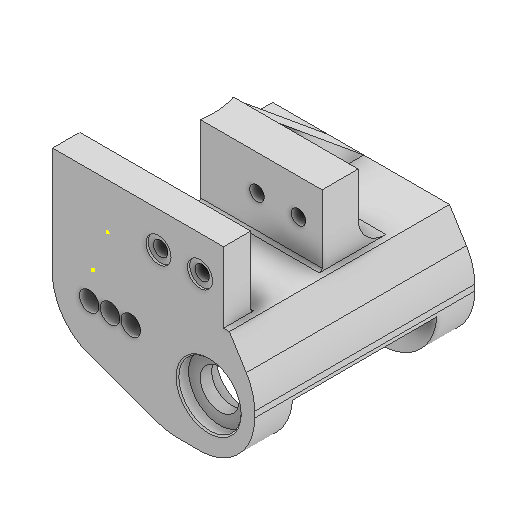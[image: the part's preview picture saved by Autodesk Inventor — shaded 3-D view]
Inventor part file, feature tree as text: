
AUTODESK INVENTOR PART (.ipt)
format: ipt  version: 2025 (Build 290162000, 162)  size: 635,392 bytes
history: native  units: in
note: dims shown in document units (in); Inventor stores cm internally (conversion verified against a paired STEP export)
features: sketch x34, extrude x32, projected_geometry x26, fillet x12, chamfer x3, reference x3, other x3, mirror x2, thicken_offset x1, plane x1, pattern_linear x1
ambient origin geometry x8: Origin, YZ Plane, XZ Plane, XY Plane, X Axis, Y Axis, Z Axis, Center Point
bodies: Solid1 (feature_tree)
feature tree (118):
  extrude  "Extrusion1"  Depth=0.25in
  extrude  "Extrusion2"  Depth=0.5512in
  extrude  "Extrusion7"  Depth=0.8809in
  extrude  "Extrusion10"  Depth=0.2165in TaperAngle=0.0deg
  extrude  "Extrusion11"  Depth=0.315in
  extrude  "Extrusion12"  TaperAngle=0.0deg  [1 undecoded]
  extrude  "Extrusion13"  Depth=0.3937in TaperAngle=0.0deg
  mirror  "Mirror1"
  fillet  "Fillet5"  Radius=0.3937in
  extrude  "Extrusion14"  Depth=0.3937in
  fillet  "Fillet6"  [1 undecoded]
  extrude  "Extrusion15"  Depth=0.3937in
  thicken_offset  "Thicken1"
  fillet  "Fillet7"  Radius=0.3858in
  extrude  "Extrusion16"  Depth=0.5118in
  extrude  "Extrusion17"  Depth=0.1969in
  fillet  "Fillet8"  Radius=1.0in
  extrude  "Extrusion18"  Depth=0.3937in
  extrude  "Extrusion19"  Depth=1.0in TaperAngle=0.0deg
  extrude  "Extrusion20"  Depth=0.315in
  extrude  "Extrusion21"  Depth=0.3228in
  extrude  "Extrusion22"  Depth=0.2756in
  extrude  "Extrusion23"  Depth=0.2047in
  plane  "Work Plane1"
  mirror  "Mirror2"
  fillet  "Fillet9"  Radius=0.2047in
  fillet  "Fillet10"  [1 undecoded]
  extrude  "Extrusion24"  Depth=0.3543in
  extrude  "Extrusion25"  Depth=0.7874in
  fillet  "Fillet12"  Radius=0.1969in
  fillet  "Fillet13"  Radius=0.1969in
  chamfer  "Chamfer1"  [1 undecoded]
  chamfer  "Chamfer2"  Distance=0.0197in Angle=45.0deg
  extrude  "Extrusion26"  Depth=0.3937in TaperAngle=0.0deg
  sketch  "Sketch27"  dims[d93=0.5in d94=0.0197in d95=0.0787in d96=45.0deg]
  extrude  "Extrusion27"  Depth=0.3937in TaperAngle=0.0deg
  extrude  "Extrusion28"  Depth=1.1811in
  extrude  "Extrusion29"  Depth=0.3937in TaperAngle=0.0deg
  pattern_linear  "Rectangular Pattern1"  Count1=2  [1 undecoded]
  extrude  "Extrusion30"  Depth=0.1969in
  extrude  "Extrusion31"  Depth=0.3937in TaperAngle=0.0deg
  extrude  "Extrusion32"  Depth=0.3937in TaperAngle=45.0deg
  fillet  "Fillet14"  Radius=0.0344in
  extrude  "Extrusion33"  TaperAngle=0.0deg  [1 undecoded]
  extrude  "Extrusion34"  TaperAngle=0.0deg  [1 undecoded]
  extrude  "Extrusion35"  TaperAngle=0.0deg  [1 undecoded]
  fillet  "Fillet15"  [1 undecoded]
  extrude  "Extrusion36"  TaperAngle=0.0deg  [1 undecoded]
  fillet  "Fillet16"  [1 undecoded]
  fillet  "Fillet18"  [1 undecoded]
  sketch  "Sketch39"  dims[d129=0.3937in d134=0.3937in d135=0.0in]
  extrude  "Extrusion38"  [1 undecoded]
  extrude  "Extrusion39"  [1 undecoded]
  chamfer  "Chamfer3"  [1 undecoded]
  sketch  "Sketch1"  dims[d1=1.005in d2=0.25in]
  sketch  "Sketch2"  dims[d3=2.0in d4=0.0in d5=0.5512in]
  projected_geometry  "Projected Loop1"
  sketch  "Sketch7"  dims[d6=0.0in d7=0.0in d21=0.8809in]
  sketch  "Sketch10"  dims[d22=0.1575in d23=0.0in d32=0.2165in d33=0.0in]
  projected_geometry  "Projected Loop7"
  sketch  "Sketch11"  dims[d34=1.1024in d35=0.315in]
  sketch  "Sketch12"  dims[d36=0.2047in d37=0.0in d38=0.0in]
  projected_geometry  "Projected Loop8"
  sketch  "Sketch13"  dims[d39=0.3937in d40=0.0in d42=1.0236in d43=0.0in d45=0.3937in]
  projected_geometry  "Projected Loop9"
  sketch  "Sketch14"  dims[d46=1.0236in d47=0.0in d48=0.3937in d49=0.0in d50=0.0in]
  projected_geometry  "Projected Loop10"
  sketch  "Sketch15"  dims[d51=0.0591in d52=0.1in d53=0.3937in d54=0.3858in]
  projected_geometry  "Projected Loop11"
  sketch  "Sketch16"  dims[d55=0.0079in d56=0.5118in]
  projected_geometry  "Projected Loop12"
  reference  "Reference1"
  sketch  "Sketch17"  dims[d57=0.2756in d58=0.1969in d59=1.0in d60=0.0in]
  projected_geometry  "Projected Loop13"
  sketch  "Sketch18"  dims[d61=1.0in d62=0.0in d63=0.3937in]
  projected_geometry  "Projected Loop14"
  reference  "Reference2"
  sketch  "Sketch19"  dims[d64=0.2047in d65=1.0in d66=0.0in]
  sketch  "Sketch20"  dims[d67=0.315in d68=0.315in]
  sketch  "Sketch21"  dims[d69=0.1969in d70=0.0in d71=0.3228in]
  sketch  "Sketch22"  dims[d72=0.315in d73=0.0in d74=0.2756in]
  reference  "Reference3"
  sketch  "Sketch23"  dims[d75=0.4724in d76=0.0in d77=0.2047in d78=0.2047in d79=0.0in d80=0.0in]
  projected_geometry  "Projected Loop15"
  sketch  "Sketch24"  dims[d81=0.3543in d82=0.3543in]
  projected_geometry  "Projected Loop16"
  projected_geometry  "Projected Loop17"
  sketch  "Sketch25"  dims[d83=0.315in d84=0.0in d85=0.7874in d86=0.1969in d88=0.1969in d89=0.0in d90=0.0in d91=0.0in]
  projected_geometry  "Projected Loop18"
  sketch  "Sketch26"  dims[d92=0.5in]
  projected_geometry  "Projected Loop19"
  sketch  "Sketch28"  dims[d97=0.1181in d98=0.0787in d99=45.0deg d100=0.3937in d101=0.0in]
  projected_geometry  "Projected Loop20"
  projected_geometry  "Projected Loop21"
  sketch  "Sketch29"  dims[d102=0.3937in d103=0.0in d104=0.3937in d105=0.0in]
  projected_geometry  "Projected Loop22"
  sketch  "Sketch30"  dims[d106=0.7874in d107=0.0in d108=1.1811in d110=0.2953in]
  projected_geometry  "Projected Loop23"
  sketch  "Sketch31"  dims[d111=0.0in d112=0.0in d113=0.3937in d114=0.0in]
  sketch  "Sketch32"  dims[d115=0.3937in d116=0.0in]
  projected_geometry  "Projected Loop24"
  sketch  "Sketch33"  dims[d117=0.0394in]
  projected_geometry  "Projected Loop25"
  projected_geometry  "Projected Loop26"
  projected_geometry  "Projected Loop27"
  sketch  "Sketch34"  dims[d118=0.3937in d119=0.0in]
  projected_geometry  "Projected Loop28"
  sketch  "Sketch35"  dims[d120=0.3937in d121=0.0in]
  projected_geometry  "Projected Loop29"
  sketch  "Sketch36"  dims[d122=0.0in d123=0.0in d124=0.7874in]
  projected_geometry  "Projected Loop30"
  sketch  "Sketch37"  dims[d125=0.2362in d126=0.0in d127=0.1969in]
  projected_geometry  "Projected Loop31"
  sketch  "Sketch40"  dims[d136=0.3937in d137=0.0in d138=0.3937in d139=0.1969in d140=45.0deg d24=0.0344in]
  sketch  "Sketch41"  dims[d27=0.0in d28=0.0in d29=0.0in d30=0.0in d87=0.0in d131=0.0in d132=0.0in d133=0.0in]
  other  "<userpath>\Desktop\puppycat\woodhouseMK1.iam"
  other  "woodhouseMK1.iam"
  other  "trackBase:1"
note: 15 required parameter values undecoded (feature->parameter linkage not recoverable at this tier; creation-order binding heuristic only, values carry confidence <= 0.55)
